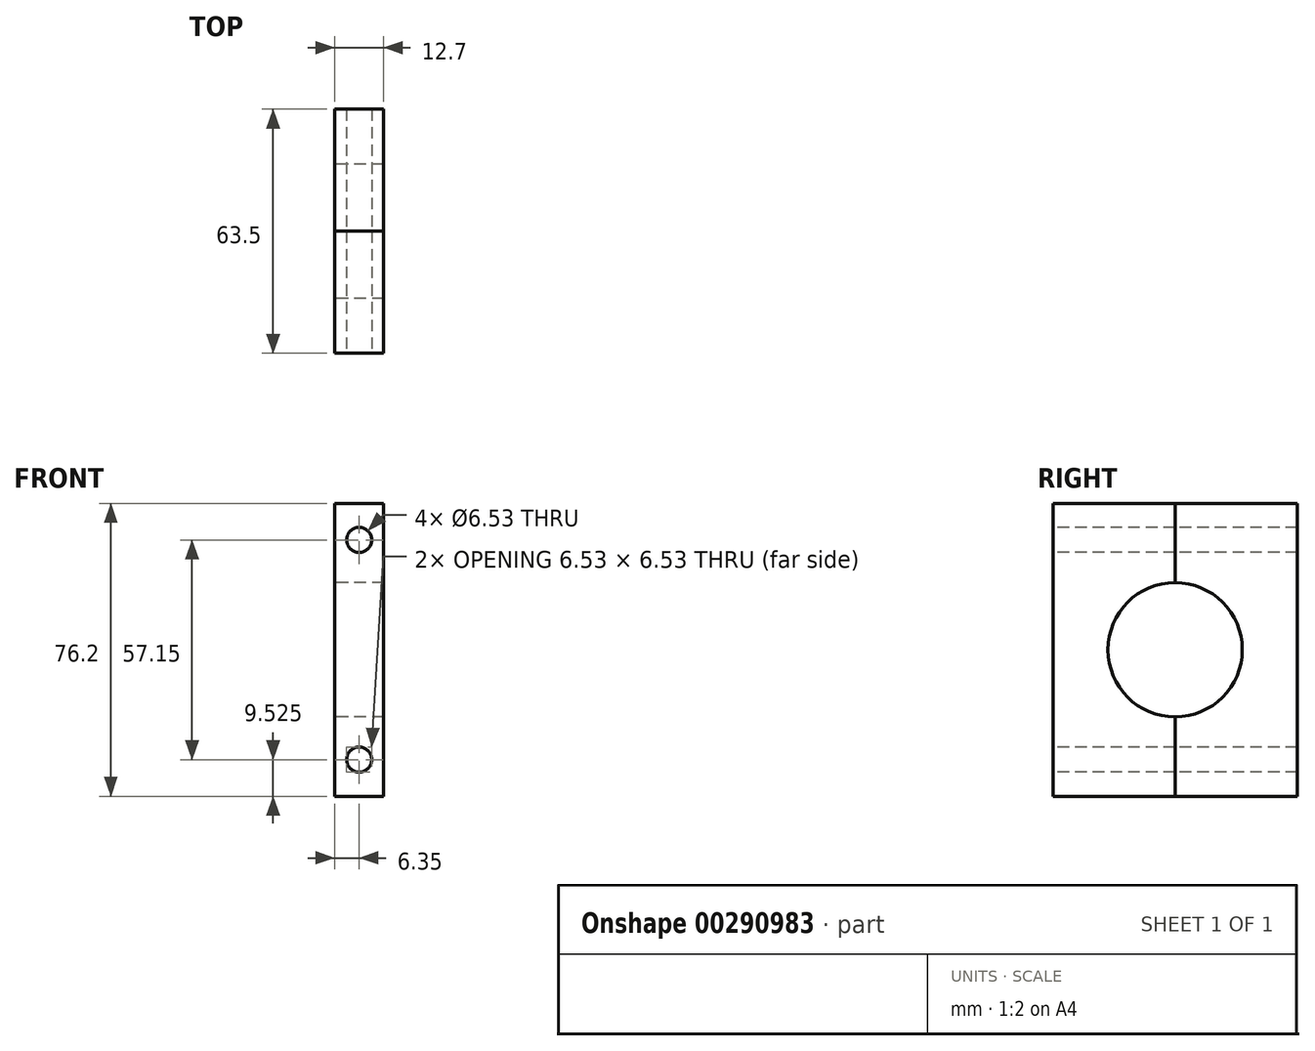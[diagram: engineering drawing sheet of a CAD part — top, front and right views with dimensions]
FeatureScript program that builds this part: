
annotation { "Feature Type Name" : "Feature", "Feature Type Description" : "" }
export const myFeature = defineFeature(function(context is Context, id is Id, definition is map)
    precondition{}
    {
        {
            var Q0;
            Q0=qCreatedBy(makeId("Right.planeOp"),FACE);
            var sketch = newSketch(context, id + "F0", { "sketchPlane" : qUnion([Q0])});
            skCircle(sketch, "E0", {"center": v(0, 0) * mm, "radius": 17.46 * mm});
            skLineSegment(sketch, "E1.bottom", {"start": v(-31.75, 38.1) * mm, "end": v(31.75, 38.1) * mm});
            skLineSegment(sketch, "E1.top", {"start": v(-31.75, -38.1) * mm, "end": v(31.75, -38.1) * mm});
            skLineSegment(sketch, "E1.left", {"start": v(-31.75, 38.1) * mm, "end": v(-31.75, -38.1) * mm});
            skLineSegment(sketch, "E1.right", {"start": v(31.75, 38.1) * mm, "end": v(31.75, -38.1) * mm});
            skLineSegment(sketch, "E2", {"start": v(0, 38.1) * mm, "end": v(0, -38.1) * mm});
            skSolve(sketch);
        }
        {
            var Q0;
            {var subQ0=sQuery(id+"F0.wireOp",EDGE,"E1.right");Q0=makeQuery(id+"F0.imprint","IMPRINT",FACE,{"disambiguationData":[TD([[makeQuery(id+"F0.imprint","IMPRINT",EDGE,{"derivedFrom":subQ0}),-1.0]])]});}
            extrude(context, id + "F1", {"entities" : qUnion([Q0]), "endBound" : BoundingType.SYMMETRIC, "depth" : 12.7 * mm});
        }
        {
            var Q0;
            {var subQ0=sQuery(id+"F0.wireOp",EDGE,"E2");Q0=makeQuery(id+"F1.opExtrude","SWEPT_FACE",FACE,{"disambiguationData":[OSD([subQ0]),TDD([makeQuery(id+"F0.imprint","IMPRINT",EDGE,{"disambiguationData":[TD([[makeQuery(id+"F0.imprint","INTERSECT",VERTEX,{"derivedFrom":[sQuery(id+"F0.wireOp",EDGE,"E1.bottom"),subQ0]}),-1.0]])],"derivedFrom":subQ0})])]});}
            var sketch = newSketch(context, id + "F2", { "sketchPlane" : qUnion([Q0])});
            skLineSegment(sketch, "E3", {"start": v(0, 28.58) * mm, "end": v(0, -28.58) * mm});
            skSolve(sketch);
        }
        {
            var Q0;
            Q0=sQuery(id+"F2.wireOp",VERTEX,"E3.start");
            var Q1;
            Q1=sQuery(id+"F2.wireOp",VERTEX,"E3.end");
            var Q2;
            Q2=makeQuery(id+"F1.opExtrude","SWEPT_BODY",BODY,{"disambiguationData":[OSD([sQuery(id+"F0.wireOp",EDGE,"E0"),sQuery(id+"F0.wireOp",EDGE,"E1.bottom"),sQuery(id+"F0.wireOp",EDGE,"E1.top"),sQuery(id+"F0.wireOp",EDGE,"E1.right"),sQuery(id+"F0.wireOp",EDGE,"E2")])]});
            hole(context, id + "F3", {"style" : HoleStyle.SIMPLE, "endStyle" : HoleEndStyle.THROUGH, "standardTappedOrClearance" : lookupTablePath({ "standard" : "ANSI", "fit" : "Close", "size" : "1/4", "type" : "Clearance" }), "standardBlindInLast" : lookupTablePath({ "fit" : "Close", "standard" : "ANSI", "size" : "1/4", "type" : "Clearance" }), "holeDiameter" : 6.53 * mm, "tappedDepth" : 12.7 * mm, "tapClearance" : 5, "startFromSketch" : true, "locations" : qUnion([Q0, Q1]), "scope" : qUnion([Q2])});
        }
        {
            var Q0;
            {var subQ0=sQuery(id+"F0.wireOp",EDGE,"E1.left");Q0=makeQuery(id+"F0.imprint","IMPRINT",FACE,{"disambiguationData":[TD([[makeQuery(id+"F0.imprint","IMPRINT",EDGE,{"derivedFrom":subQ0}),1.0]])]});}
            extrude(context, id + "F4", {"entities" : qUnion([Q0]), "endBound" : BoundingType.SYMMETRIC, "depth" : 12.7 * mm});
        }
        {
            var Q0;
            Q0=makeQuery(id+"F4.opExtrude","SWEPT_FACE",FACE,{"disambiguationData":[OSD([sQuery(id+"F0.wireOp",EDGE,"E1.left")])]});
            var sketch = newSketch(context, id + "F5", { "sketchPlane" : qUnion([Q0])});
            skPoint(sketch, "E4", {"position": v(0, 28.58) * mm});
            skPoint(sketch, "E5", {"position": v(0, -28.58) * mm});
            skSolve(sketch);
        }
        {
            var Q0;
            Q0=sQuery(id+"F5.wireOp",VERTEX,"E4");
            var Q1;
            Q1=sQuery(id+"F5.wireOp",VERTEX,"E5");
            var Q2;
            Q2=makeQuery(id+"F4.opExtrude","SWEPT_BODY",BODY,{"disambiguationData":[OSD([sQuery(id+"F0.wireOp",EDGE,"E0"),sQuery(id+"F0.wireOp",EDGE,"E1.bottom"),sQuery(id+"F0.wireOp",EDGE,"E1.top"),sQuery(id+"F0.wireOp",EDGE,"E1.left"),sQuery(id+"F0.wireOp",EDGE,"E2")])]});
            hole(context, id + "F6", {"style" : HoleStyle.SIMPLE, "endStyle" : HoleEndStyle.THROUGH, "standardTappedOrClearance" : lookupTablePath({ "standard" : "ANSI", "fit" : "Close", "size" : "1/4", "type" : "Clearance" }), "standardBlindInLast" : lookupTablePath({ "fit" : "Close", "standard" : "ANSI", "size" : "1/4", "type" : "Clearance" }), "holeDiameter" : 6.53 * mm, "tappedDepth" : 12.7 * mm, "tapClearance" : 5, "startFromSketch" : true, "locations" : qUnion([Q0, Q1]), "scope" : qUnion([Q2])});
        }
    });
